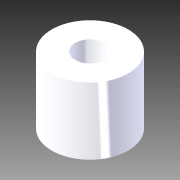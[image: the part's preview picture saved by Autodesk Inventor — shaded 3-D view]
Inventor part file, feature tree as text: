
AUTODESK INVENTOR PART (.ipt)
format: ipt  version: 2012 (Build 160160000, 160)  size: 84,480 bytes
history: native  units: in
note: dims shown in document units (in); Inventor stores cm internally (conversion verified against a paired STEP export)
features: other x1, imported_body x1, plane x1, split x1
ambient origin geometry x8: Origin, YZ Plane, XZ Plane, XY Plane, X Axis, Y Axis, Z Axis, Center Point
feature tree (4):
  parser-record x1  (decoder bookkeeping rows leaked as tree rows — omitted from the tree; the rows remain in map.json)
  imported_body  "Base1"
  plane  "Work Plane1"
  split  "Split1"
